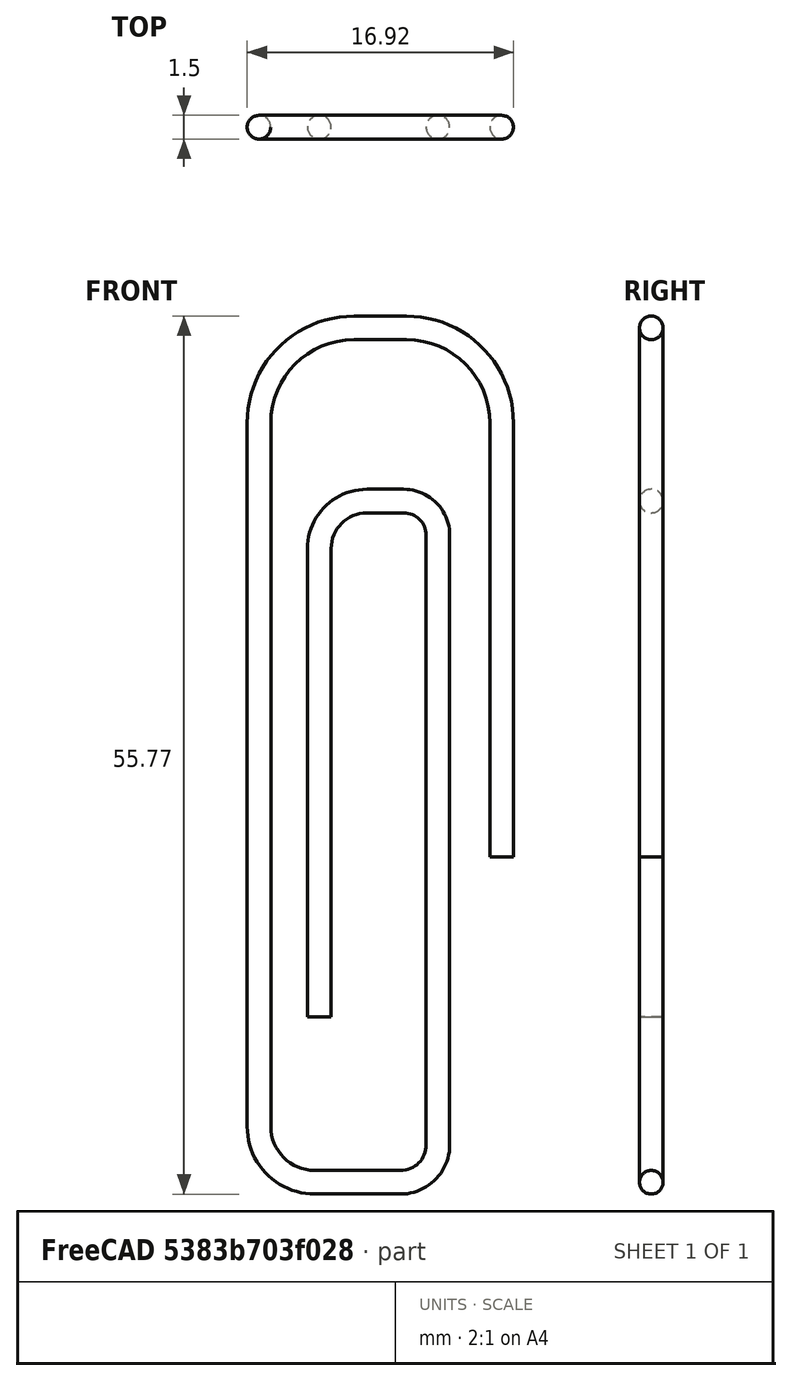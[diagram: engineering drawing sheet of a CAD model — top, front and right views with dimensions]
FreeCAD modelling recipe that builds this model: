
FCSTD DOCUMENT  (FreeCAD 0.21R33771 (Git))
Label: paperclip
License: All rights reserved
LicenseURL: http://en.wikipedia.org/wiki/All_rights_reserved
objects: Sketcher::SketchObject×2, PartDesign::AdditivePipe×1, PartDesign::Body×1
note: 5 computed .brp shape members not serialized (recipe doc carries the construction recipe); baked Part::Feature solids carry a one-line shape summary decoded from their .brp

FEATURE [Sketcher::SketchObject] Sketch
  FullyConstrained = false
  MapMode = 5
  Placement = pos=(0,0,0) rot=(1,0,0;1.5708rad)
  Support = -> [XZ_Plane]
  sketch-geometry (13):
    g0: LineSegment StartX=11.1741 StartY=-6.07321 StartZ=0 EndX=11.1741 EndY=21.4881 EndZ=0
    g1: LineSegment StartX=5.17411 StartY=27.4881 StartZ=0 EndX=1.82604 EndY=27.4881 EndZ=0
    g2: LineSegment StartX=-4.17396 StartY=21.4881 StartZ=0 EndX=-4.17396 EndY=-23.2055 EndZ=0
    g3: LineSegment StartX=-0.666413 StartY=-26.7131 StartZ=0 EndX=4.78917 EndY=-26.7131 EndZ=0
    g4: LineSegment StartX=7.1261 StartY=-24.3762 StartZ=0 EndX=7.1261 EndY=14.3468 EndZ=0
    g5: LineSegment StartX=4.9819 StartY=16.491 StartZ=0 EndX=2.64722 EndY=16.491 EndZ=0
    g6: LineSegment StartX=-0.341284 StartY=13.5025 StartZ=0 EndX=-0.341284 EndY=-16.2265 EndZ=0
    g7: ArcOfCircle CenterX=1.82604 CenterY=21.4881 CenterZ=0 NormalX=0 NormalY=0 NormalZ=1 AngleXU=0 Radius=6 StartAngle=1.5708 EndAngle=3.14159
    g8: ArcOfCircle CenterX=5.17411 CenterY=21.4881 CenterZ=0 NormalX=0 NormalY=0 NormalZ=1 AngleXU=0 Radius=6 StartAngle=2e-16 EndAngle=1.5708
    g9: ArcOfCircle CenterX=2.64722 CenterY=13.5025 CenterZ=0 NormalX=0 NormalY=0 NormalZ=1 AngleXU=0 Radius=2.9885 StartAngle=1.5708 EndAngle=3.14159
    g10: ArcOfCircle CenterX=4.9819 CenterY=14.3468 CenterZ=0 NormalX=0 NormalY=0 NormalZ=1 AngleXU=0 Radius=2.14419 StartAngle=0 EndAngle=1.5708
    g11: ArcOfCircle CenterX=-0.666413 CenterY=-23.2055 CenterZ=0 NormalX=0 NormalY=0 NormalZ=1 AngleXU=0 Radius=3.50755 StartAngle=3.14159 EndAngle=4.71239
    g12: ArcOfCircle CenterX=4.78917 CenterY=-24.3762 CenterZ=0 NormalX=0 NormalY=0 NormalZ=1 AngleXU=0 Radius=2.33692 StartAngle=4.71239 EndAngle=6.28319
  constraints (21):
    c: Vertical(g0)
    c: Horizontal(g1)
    c: Vertical(g2)
    c: Vertical(g4)
    c: Horizontal(g5)
    c: Vertical(g6)
    c: Horizontal(g3)
    c: Tangent(g2,g7) = -1.5708
    c: Tangent(g1,g7) = -1.5708
    c: Tangent(g1,g8) = -1.5708
    c: Tangent(g0,g8) = -1.5708
    c: Tangent(g6,g9) = -1.5708
    c: Tangent(g5,g9) = -1.5708
    c: Tangent(g5,g10) = -1.5708
    c: Tangent(g4,g10) = -1.5708
    c: Radius(g8) = 6
    c: Radius(g7) = 6
    c: Tangent(g2,g11) = -1.5708
    c: Tangent(g3,g11) = -1.5708
    c: Tangent(g4,g12) = -1.5708
    c: Tangent(g3,g12) = -1.5708
FEATURE [Sketcher::SketchObject] Sketch001
  FullyConstrained = false
  MapMode = 5
  Support = -> [XY_Plane]
  sketch-geometry (1):
    g0: Circle CenterX=-4.20646 CenterY=0 CenterZ=0 NormalX=0 NormalY=0 NormalZ=1 AngleXU=0 Radius=0.75
  constraints (2):
    c: PointOnObject(g0,g-1)
    c: Radius(g0) = 0.75
FEATURE [PartDesign::AdditivePipe] AdditivePipe
  AuxilleryCurvelinear = true
  AuxillerySpineTangent = false
  Binormal = (0,0,0)
  Mode = 0
  Profile = -> Sketch001
  Refine = true
  Spine = -> Sketch
  SpineTangent = false
  Transformation = 0
  Transition = 0
FEATURE [PartDesign::Body] Body
  Group = -> [Sketch,Sketch001,AdditivePipe]
  Origin = -> Origin
  Tip = -> AdditivePipe
